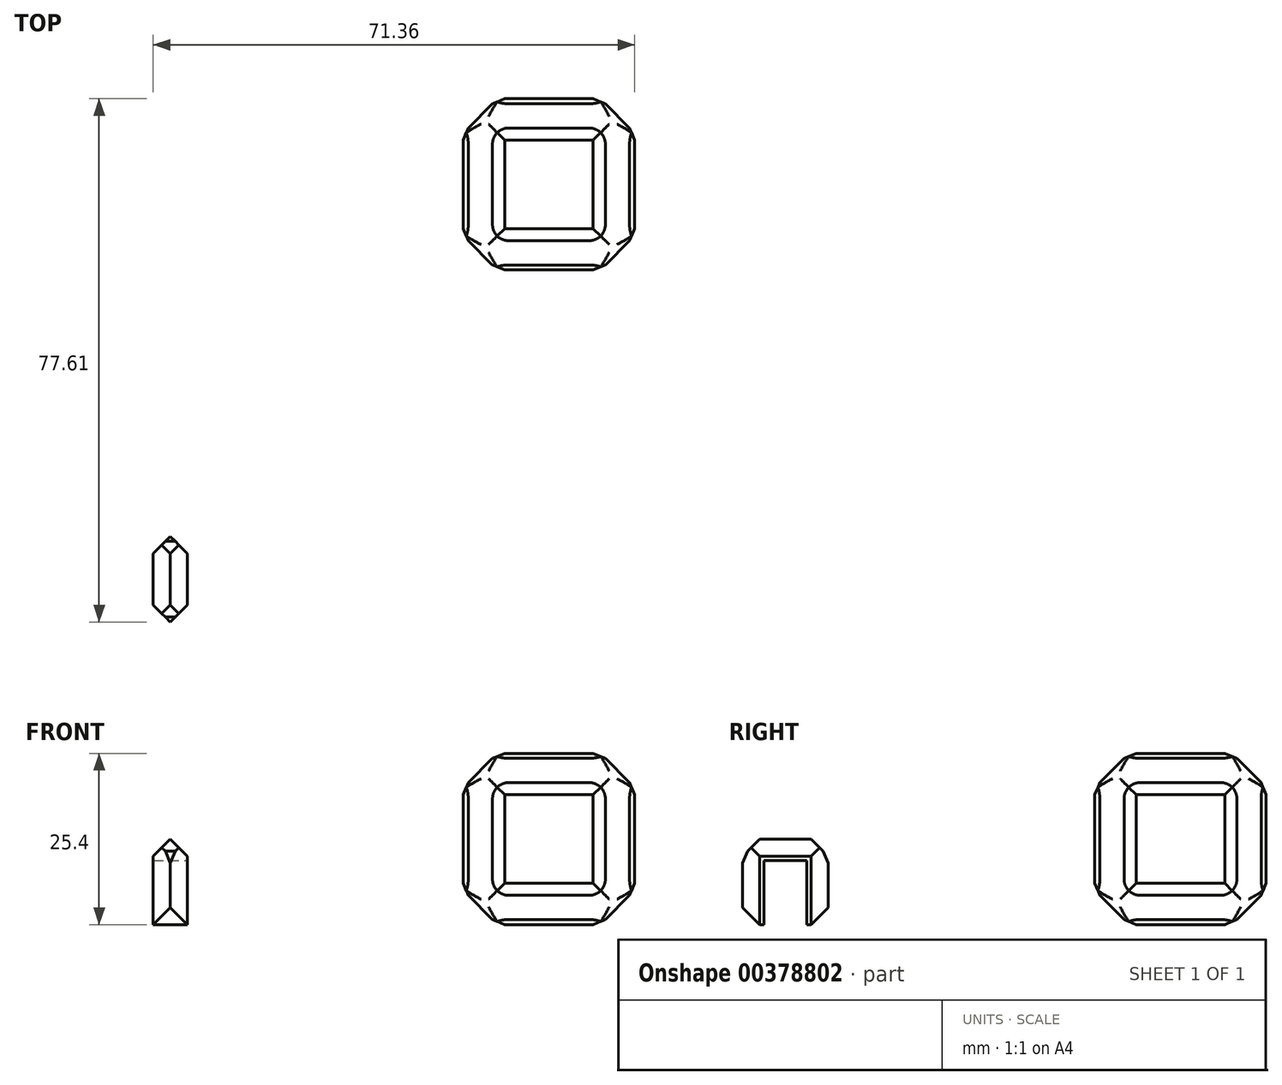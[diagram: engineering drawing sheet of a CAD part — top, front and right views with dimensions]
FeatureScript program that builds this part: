
annotation { "Feature Type Name" : "Feature", "Feature Type Description" : "" }
export const myFeature = defineFeature(function(context is Context, id is Id, definition is map)
    precondition{}
    {
        {
            var Q0;
            Q0=qCreatedBy(makeId("Top.planeOp"),FACE);
            var sketch = newSketch(context, id + "F0", { "sketchPlane" : qUnion([Q0])});
            skLineSegment(sketch, "E0.bottom", {"start": v(0, -1.6) * mm, "end": v(25.4, -1.6) * mm});
            skLineSegment(sketch, "E0.top", {"start": v(0, 23.8) * mm, "end": v(25.4, 23.8) * mm});
            skLineSegment(sketch, "E0.left", {"start": v(0, -1.6) * mm, "end": v(0, 23.8) * mm});
            skLineSegment(sketch, "E0.right", {"start": v(25.4, -1.6) * mm, "end": v(25.4, 23.8) * mm});
            skSolve(sketch);
        }
        {
            var Q0;
            Q0=makeQuery(id+"F0.imprint","IMPRINT",FACE,{"disambiguationData":[TD([[makeQuery(id+"F0.imprint","IMPRINT",EDGE,{"derivedFrom":sQuery(id+"F0.wireOp",EDGE,"E0.bottom")}),1.0]])]});
            extrude(context, id + "F1", {"entities" : qUnion([Q0]), "depth" : 25.4 * mm});
        }
        {
            var Q0;
            Q0=makeQuery(id+"F1.opExtrude","CAP_FACE",FACE,{"disambiguationData":[OSD([sQuery(id+"F0.wireOp",EDGE,"E0.bottom"),sQuery(id+"F0.wireOp",EDGE,"E0.top"),sQuery(id+"F0.wireOp",EDGE,"E0.left"),sQuery(id+"F0.wireOp",EDGE,"E0.right")])],"isStart":false});
            var Q1;
            Q1=makeQuery(id+"F1.opExtrude","SWEPT_FACE",FACE,{"disambiguationData":[OSD([sQuery(id+"F0.wireOp",EDGE,"E0.right")])]});
            var Q2;
            Q2=makeQuery(id+"F1.opExtrude","SWEPT_FACE",FACE,{"disambiguationData":[OSD([sQuery(id+"F0.wireOp",EDGE,"E0.bottom")])]});
            var Q3;
            Q3=makeQuery(id+"F1.opExtrude","SWEPT_FACE",FACE,{"disambiguationData":[OSD([sQuery(id+"F0.wireOp",EDGE,"E0.left")])]});
            var Q4;
            Q4=makeQuery(id+"F1.opExtrude","SWEPT_FACE",FACE,{"disambiguationData":[OSD([sQuery(id+"F0.wireOp",EDGE,"E0.top")])]});
            chamfer(context, id + "F2", {"entities" : qUnion([Q0, Q1, Q2, Q3, Q4]), "width" : 5.08 * mm, "tangentPropagation" : true});
        }
        {
            var Q0;
            Q0=makeQuery(id+"F1.opExtrude","CAP_FACE",FACE,{"disambiguationData":[OSD([sQuery(id+"F0.wireOp",EDGE,"E0.bottom"),sQuery(id+"F0.wireOp",EDGE,"E0.top"),sQuery(id+"F0.wireOp",EDGE,"E0.left"),sQuery(id+"F0.wireOp",EDGE,"E0.right")])],"isStart":true});
            var Q1;
            Q1=makeQuery(id+"F1.opExtrude","SWEPT_FACE",FACE,{"disambiguationData":[OSD([sQuery(id+"F0.wireOp",EDGE,"E0.right")])]});
            var Q2;
            Q2=makeQuery(id+"F1.opExtrude","SWEPT_FACE",FACE,{"disambiguationData":[OSD([sQuery(id+"F0.wireOp",EDGE,"E0.bottom")])]});
            var Q3;
            Q3=makeQuery(id+"F1.opExtrude","CAP_FACE",FACE,{"disambiguationData":[OSD([sQuery(id+"F0.wireOp",EDGE,"E0.bottom"),sQuery(id+"F0.wireOp",EDGE,"E0.top"),sQuery(id+"F0.wireOp",EDGE,"E0.left"),sQuery(id+"F0.wireOp",EDGE,"E0.right")])],"isStart":false});
            var Q4;
            Q4=makeQuery(id+"F1.opExtrude","SWEPT_FACE",FACE,{"disambiguationData":[OSD([sQuery(id+"F0.wireOp",EDGE,"E0.left")])]});
            var Q5;
            Q5=makeQuery(id+"F1.opExtrude","SWEPT_FACE",FACE,{"disambiguationData":[OSD([sQuery(id+"F0.wireOp",EDGE,"E0.top")])]});
            chamfer(context, id + "F3", {"entities" : qUnion([Q0, Q1, Q2, Q3, Q4, Q5]), "width" : 2.54 * mm, "tangentPropagation" : true});
        }
        {
            var Q0;
            {var subQ0=sQuery(id+"F0.wireOp",EDGE,"E0.left");var subQ1=sQuery(id+"F0.wireOp",EDGE,"E0.top");Q0=makeQuery(id+"F2.opChamfer","BLEND_FACE",FACE,{"disambiguationData":[OSD([subQ1,subQ0]),TDD([makeQuery(id+"F1.opExtrude","CAP_VERTEX",VERTEX,{"disambiguationData":[OSD([subQ1,subQ0])],"isStart":false})])]});}
            var Q1;
            {var subQ0=sQuery(id+"F0.wireOp",EDGE,"E0.left");var subQ1=sQuery(id+"F0.wireOp",EDGE,"E0.bottom");Q1=makeQuery(id+"F2.opChamfer","BLEND_FACE",FACE,{"disambiguationData":[OSD([subQ1,subQ0]),TDD([makeQuery(id+"F1.opExtrude","CAP_VERTEX",VERTEX,{"disambiguationData":[OSD([subQ1,subQ0])],"isStart":false})])]});}
            var Q2;
            {var subQ0=sQuery(id+"F0.wireOp",EDGE,"E0.right");var subQ1=sQuery(id+"F0.wireOp",EDGE,"E0.bottom");Q2=makeQuery(id+"F2.opChamfer","BLEND_FACE",FACE,{"disambiguationData":[OSD([subQ1,subQ0]),TDD([makeQuery(id+"F1.opExtrude","CAP_VERTEX",VERTEX,{"disambiguationData":[OSD([subQ1,subQ0])],"isStart":false})])]});}
            var Q3;
            {var subQ0=sQuery(id+"F0.wireOp",EDGE,"E0.right");var subQ1=sQuery(id+"F0.wireOp",EDGE,"E0.top");Q3=makeQuery(id+"F2.opChamfer","BLEND_FACE",FACE,{"disambiguationData":[OSD([subQ1,subQ0]),TDD([makeQuery(id+"F1.opExtrude","CAP_VERTEX",VERTEX,{"disambiguationData":[OSD([subQ1,subQ0])],"isStart":false})])]});}
            var Q4;
            {var subQ0=sQuery(id+"F0.wireOp",EDGE,"E0.right");var subQ1=sQuery(id+"F0.wireOp",EDGE,"E0.top");Q4=makeQuery(id+"F2.opChamfer","BLEND_FACE",FACE,{"disambiguationData":[OSD([subQ1,subQ0]),TDD([makeQuery(id+"F1.opExtrude","CAP_VERTEX",VERTEX,{"disambiguationData":[OSD([subQ1,subQ0])],"isStart":true})])]});}
            var Q5;
            {var subQ0=sQuery(id+"F0.wireOp",EDGE,"E0.left");var subQ1=sQuery(id+"F0.wireOp",EDGE,"E0.top");Q5=makeQuery(id+"F2.opChamfer","BLEND_FACE",FACE,{"disambiguationData":[OSD([subQ1,subQ0]),TDD([makeQuery(id+"F1.opExtrude","CAP_VERTEX",VERTEX,{"disambiguationData":[OSD([subQ1,subQ0])],"isStart":true})])]});}
            var Q6;
            {var subQ0=sQuery(id+"F0.wireOp",EDGE,"E0.left");var subQ1=sQuery(id+"F0.wireOp",EDGE,"E0.bottom");Q6=makeQuery(id+"F2.opChamfer","BLEND_FACE",FACE,{"disambiguationData":[OSD([subQ1,subQ0]),TDD([makeQuery(id+"F1.opExtrude","CAP_VERTEX",VERTEX,{"disambiguationData":[OSD([subQ1,subQ0])],"isStart":true})])]});}
            var Q7;
            {var subQ0=sQuery(id+"F0.wireOp",EDGE,"E0.right");var subQ1=sQuery(id+"F0.wireOp",EDGE,"E0.bottom");Q7=makeQuery(id+"F2.opChamfer","BLEND_FACE",FACE,{"disambiguationData":[OSD([subQ1,subQ0]),TDD([makeQuery(id+"F1.opExtrude","CAP_VERTEX",VERTEX,{"disambiguationData":[OSD([subQ1,subQ0])],"isStart":true})])]});}
            fillet(context, id + "F4", {"entities" : qUnion([Q0, Q1, Q2, Q3, Q4, Q5, Q6, Q7]), "radius" : 5.08 * mm, "tangentPropagation" : true, "allowEdgeOverflow" : false});
        }
        {
            var Q0;
            Q0=qCreatedBy(makeId("Top.planeOp"),FACE);
            var sketch = newSketch(context, id + "F5", { "sketchPlane" : qUnion([Q0])});
            skLineSegment(sketch, "E1.bottom", {"start": v(-40.88, -53.8) * mm, "end": v(-45.96, -53.8) * mm});
            skLineSegment(sketch, "E1.top", {"start": v(-40.88, -41.1) * mm, "end": v(-45.96, -41.1) * mm});
            skLineSegment(sketch, "E1.left", {"start": v(-40.88, -53.8) * mm, "end": v(-40.88, -41.1) * mm});
            skLineSegment(sketch, "E1.right", {"start": v(-45.96, -53.8) * mm, "end": v(-45.96, -41.1) * mm});
            skSolve(sketch);
        }
        {
            var Q0;
            Q0=makeQuery(id+"F5.imprint","IMPRINT",FACE,{"disambiguationData":[TD([[makeQuery(id+"F5.imprint","IMPRINT",EDGE,{"derivedFrom":sQuery(id+"F5.wireOp",EDGE,"E1.bottom")}),-1.0]])]});
            extrude(context, id + "F6", {"entities" : qUnion([Q0]), "depth" : 12.7 * mm});
        }
        {
            var Q0;
            Q0=makeQuery(id+"F6.opExtrude","SWEPT_FACE",FACE,{"disambiguationData":[OSD([sQuery(id+"F5.wireOp",EDGE,"E1.left")])]});
            var sketch = newSketch(context, id + "F7", { "sketchPlane" : qUnion([Q0])});
            skLineSegment(sketch, "E2", {"start": v(-50.63, 0) * mm, "end": v(-50.63, 9.53) * mm});
            skLineSegment(sketch, "E3", {"start": v(-50.63, 9.53) * mm, "end": v(-44.28, 9.53) * mm});
            skLineSegment(sketch, "E4", {"start": v(-44.28, 0) * mm, "end": v(-44.28, 9.53) * mm});
            skPoint(sketch, "E5.orphan", {"position": v(-53.8, 9.53) * mm});
            skPoint(sketch, "E6.start.orphan", {"position": v(-50.63, 12.7) * mm});
            skPoint(sketch, "E7.orphan", {"position": v(-44.28, 12.7) * mm});
            skPoint(sketch, "E8.orphan", {"position": v(-53.8, 12.7) * mm});
            skPoint(sketch, "E9.end.orphan", {"position": v(-53.8, 6.35) * mm});
            skPoint(sketch, "E10.orphan", {"position": v(-47.46, 0) * mm});
            skPoint(sketch, "E11.end.orphan", {"position": v(-53.8, 0) * mm});
            skPoint(sketch, "E12.end.orphan", {"position": v(-41.1, 0) * mm});
            skSolve(sketch);
        }
        {
            var Q0;
            {var subQ0=sQuery(id+"F7.wireOp",EDGE,"E2");Q0=makeQuery(id+"F7.imprint","IMPRINT",FACE,{"disambiguationData":[TD([[makeQuery(id+"F7.imprint","IMPRINT",EDGE,{"derivedFrom":subQ0}),-1.0]])]});}
            extrude(context, id + "F8", {"entities" : qUnion([Q0]), "operationType" : NewBodyOperationType.REMOVE, "oppositeDirection" : true, "depth" : 5.08 * mm});
        }
        {
            var Q0;
            Q0=makeQuery(id+"F6.opExtrude","CAP_FACE",FACE,{"disambiguationData":[OSD([sQuery(id+"F5.wireOp",EDGE,"E1.bottom"),sQuery(id+"F5.wireOp",EDGE,"E1.top"),sQuery(id+"F5.wireOp",EDGE,"E1.left"),sQuery(id+"F5.wireOp",EDGE,"E1.right")])],"isStart":false});
            chamfer(context, id + "F9", {"entities" : qUnion([Q0]), "width" : 2.54 * mm, "tangentPropagation" : true});
        }
        {
            var Q0;
            Q0=makeQuery(id+"F6.opExtrude","SWEPT_FACE",FACE,{"disambiguationData":[OSD([sQuery(id+"F5.wireOp",EDGE,"E1.bottom")])]});
            var Q1;
            Q1=makeQuery(id+"F6.opExtrude","SWEPT_FACE",FACE,{"disambiguationData":[OSD([sQuery(id+"F5.wireOp",EDGE,"E1.top")])]});
            chamfer(context, id + "F10", {"entities" : qUnion([Q0, Q1]), "width" : 2.54 * mm, "tangentPropagation" : true});
        }
    });
